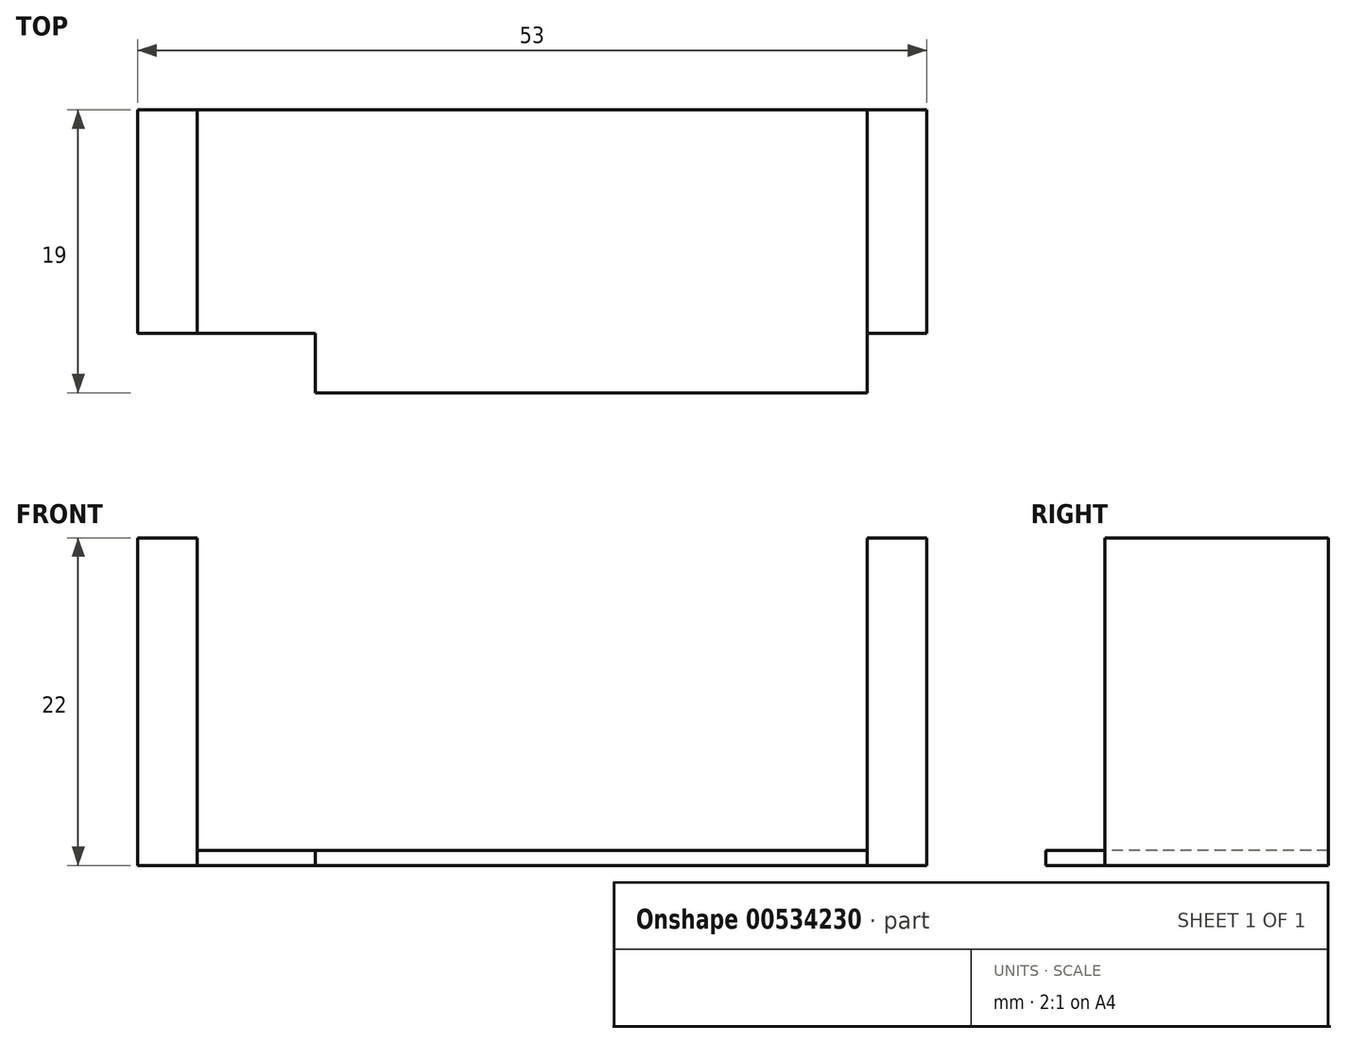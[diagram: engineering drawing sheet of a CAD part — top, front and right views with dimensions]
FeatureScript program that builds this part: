
annotation { "Feature Type Name" : "Feature", "Feature Type Description" : "" }
export const myFeature = defineFeature(function(context is Context, id is Id, definition is map)
    precondition{}
    {
        {
            var Q0;
            Q0=qCreatedBy(makeId("Top.planeOp"),FACE);
            var sketch = newSketch(context, id + "F0", { "sketchPlane" : qUnion([Q0])});
            skLineSegment(sketch, "E0.left", {"start": v(-7.93, 12.62) * mm, "end": v(-7.93, -2.38) * mm});
            skLineSegment(sketch, "E1.left", {"start": v(37.07, -6.38) * mm, "end": v(37.07, 8.62) * mm});
            skLineSegment(sketch, "E2.bottom", {"start": v(-7.93, -2.38) * mm, "end": v(-11.93, -2.38) * mm});
            skLineSegment(sketch, "E2.top", {"start": v(-7.93, 12.62) * mm, "end": v(-11.93, 12.62) * mm});
            skLineSegment(sketch, "E2.left", {"start": v(-7.93, -2.38) * mm, "end": v(-7.93, 12.62) * mm});
            skLineSegment(sketch, "E2.right", {"start": v(-11.93, -2.38) * mm, "end": v(-11.93, 12.62) * mm});
            skLineSegment(sketch, "E3.bottom", {"start": v(-7.93, 12.62) * mm, "end": v(37.07, 12.62) * mm});
            skLineSegment(sketch, "E3.top", {"start": v(-7.93, -6.38) * mm, "end": v(37.07, -6.38) * mm});
            skLineSegment(sketch, "E3.left", {"start": v(-7.93, 12.62) * mm, "end": v(-7.93, -6.38) * mm, "construction": true});
            skLineSegment(sketch, "E3.right", {"start": v(37.07, 12.62) * mm, "end": v(37.07, -6.38) * mm});
            skPoint(sketch, "E4", {"position": v(37.07, -2.38) * mm});
            skLineSegment(sketch, "E5.bottom", {"start": v(37.07, -2.38) * mm, "end": v(37.07, -2.38) * mm});
            skLineSegment(sketch, "E5.top", {"start": v(37.07, 12.62) * mm, "end": v(37.07, 12.62) * mm});
            skLineSegment(sketch, "E5.left", {"start": v(37.07, -2.38) * mm, "end": v(37.07, 12.62) * mm});
            skLineSegment(sketch, "E5.right", {"start": v(37.07, -2.38) * mm, "end": v(37.07, 12.62) * mm});
            skLineSegment(sketch, "E6.bottom", {"start": v(37.07, 12.62) * mm, "end": v(41.07, 12.62) * mm});
            skLineSegment(sketch, "E6.top", {"start": v(37.07, -2.38) * mm, "end": v(41.07, -2.38) * mm});
            skLineSegment(sketch, "E6.left", {"start": v(37.07, 12.62) * mm, "end": v(37.07, -2.38) * mm});
            skLineSegment(sketch, "E6.right", {"start": v(41.07, 12.62) * mm, "end": v(41.07, -2.38) * mm});
            skLineSegment(sketch, "E7", {"start": v(-7.93, -6.38) * mm, "end": v(-7.93, 12.62) * mm});
            skLineSegment(sketch, "E8.bottom", {"start": v(-19.2, -2.38) * mm, "end": v(0, -2.38) * mm});
            skLineSegment(sketch, "E8.top", {"start": v(-19.2, -21.9) * mm, "end": v(0, -21.9) * mm});
            skLineSegment(sketch, "E8.left", {"start": v(-19.2, -2.38) * mm, "end": v(-19.2, -21.9) * mm});
            skLineSegment(sketch, "E8.right", {"start": v(0, -2.38) * mm, "end": v(0, -21.9) * mm});
            skSolve(sketch);
        }
        {
            var Q0;
            {var subQ0=sQuery(id+"F0.wireOp",EDGE,"E2.bottom");Q0=makeQuery(id+"F0.imprint","IMPRINT",FACE,{"disambiguationData":[TD([[makeQuery(id+"F0.imprint","IMPRINT",EDGE,{"derivedFrom":subQ0}),-1.0]])]});}
            var Q1;
            {var subQ3=sQuery(id+"F0.wireOp",EDGE,"E6.bottom");Q1=makeQuery(id+"F0.imprint","IMPRINT",FACE,{"disambiguationData":[TD([[makeQuery(id+"F0.imprint","IMPRINT",EDGE,{"derivedFrom":subQ3}),-1.0]])]});}
            extrude(context, id + "F1", {"entities" : qUnion([Q0, Q1]), "depth" : 22 * mm, "offsetDistance" : 25 * mm});
        }
        {
            var Q0;
            {var subQ3=sQuery(id+"F0.wireOp",EDGE,"E3.bottom");Q0=makeQuery(id+"F0.imprint","IMPRINT",FACE,{"disambiguationData":[TD([[makeQuery(id+"F0.imprint","IMPRINT",EDGE,{"derivedFrom":subQ3}),-1.0]])]});}
            extrude(context, id + "F2", {"entities" : qUnion([Q0]), "depth" : 1 * mm, "offsetDistance" : 25 * mm});
        }
    });
